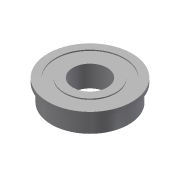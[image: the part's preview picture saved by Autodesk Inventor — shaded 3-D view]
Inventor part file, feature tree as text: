
AUTODESK INVENTOR PART (.ipt)
format: ipt  version: 2013 (Build 170138000, 138)  size: 115,200 bytes
history: native  units: in
note: dims shown in document units (in); Inventor stores cm internally (conversion verified against a paired STEP export)
features: revolve x1, imported_body x1
ambient origin geometry x8: Origin, YZ Plane, XZ Plane, XY Plane, X Axis, Y Axis, Z Axis, Center Point
feature tree (2):
  revolve  "Revolve1"  [1 undecoded]
  imported_body  "Base1"
note: 1 required parameter value undecoded (feature->parameter linkage not recoverable at this tier; creation-order binding heuristic only, values carry confidence <= 0.55)
